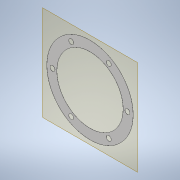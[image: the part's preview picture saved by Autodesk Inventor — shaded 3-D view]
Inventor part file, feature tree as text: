
AUTODESK INVENTOR PART (.ipt)
format: ipt  version: 2020 (Build 240168000, 168)  size: 116,224 bytes
history: native  units: mm
features: other x3, plane x1, extrude x1, sketch x1, reference x1
ambient origin geometry x8: Origin, YZ Plane, XZ Plane, XY Plane, X Axis, Y Axis, Z Axis, Center Point
bodies: 实体1 (feature_tree)
feature tree (7):
  plane  "工作平面1"
  extrude  "拉伸1"  [1 undecoded]
  sketch  "草图1"  dims[d0=0.18mm d1=0.0mm]
  reference  "参考1"
  other  "<userpath>\Desktop\ME_course_project\课设试试\shaft_try_1.iam"
  other  "shaft_try_1.iam"
  other  "轴承端盖2:1"
note: 1 required parameter value undecoded (feature->parameter linkage not recoverable at this tier; creation-order binding heuristic only, values carry confidence <= 0.55)
